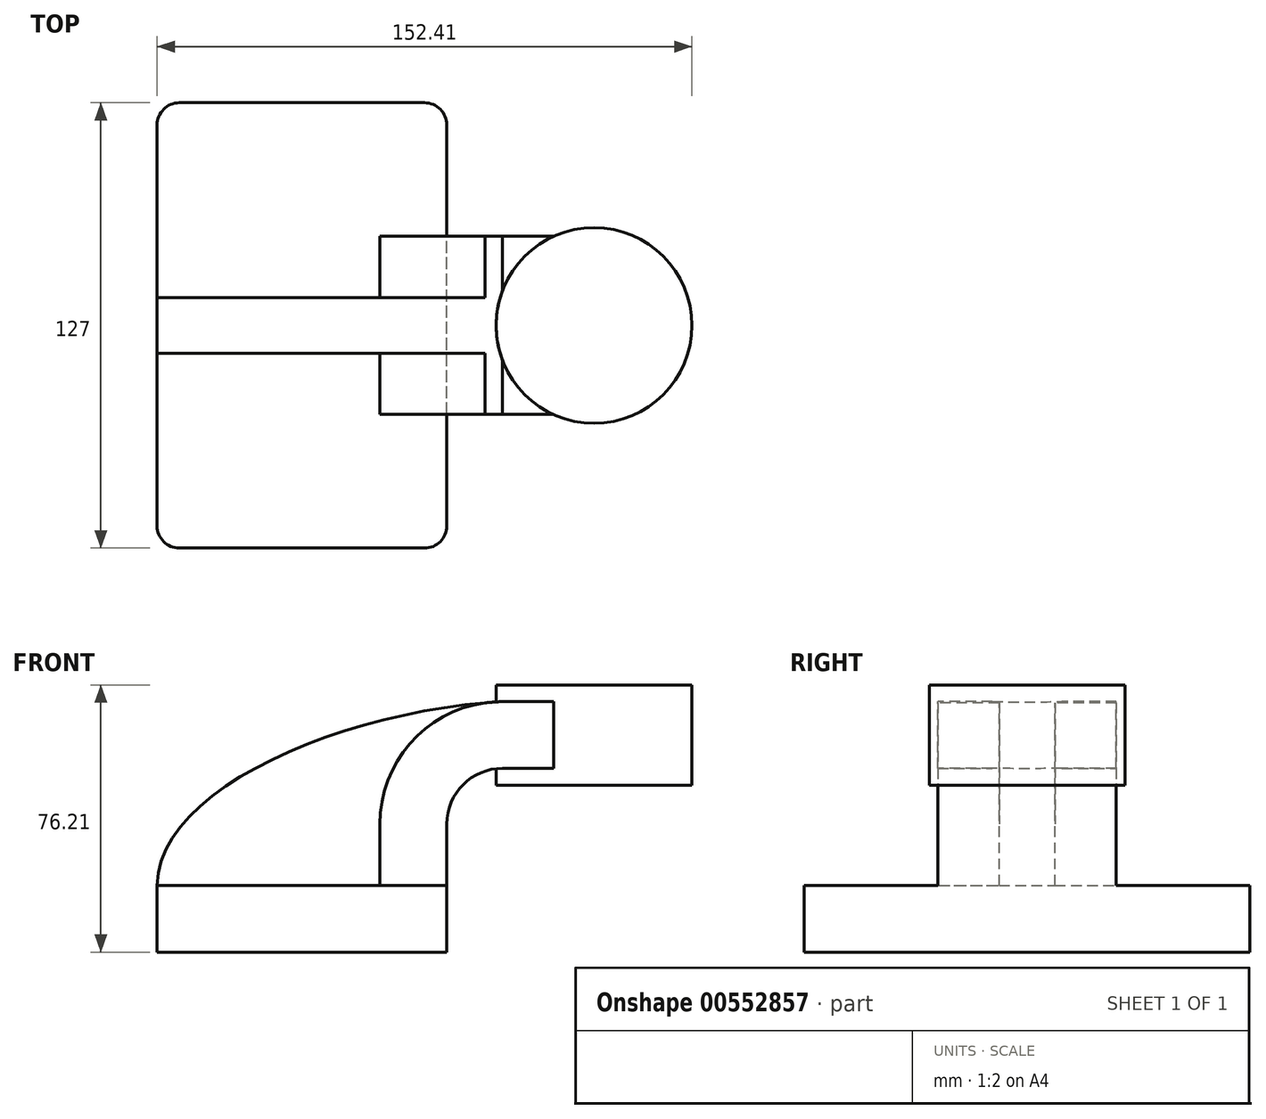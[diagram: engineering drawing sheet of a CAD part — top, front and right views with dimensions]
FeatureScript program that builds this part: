
annotation { "Feature Type Name" : "Feature", "Feature Type Description" : "" }
export const myFeature = defineFeature(function(context is Context, id is Id, definition is map)
    precondition{}
    {
        {
            var Q0;
            Q0=qCreatedBy(makeId("Front.planeOp"),FACE);
            var sketch = newSketch(context, id + "F0", { "sketchPlane" : qUnion([Q0])});
            skLineSegment(sketch, "E0.bottom", {"start": v(-41.28, 9.52) * mm, "end": v(41.27, 9.53) * mm});
            skLineSegment(sketch, "E0.top", {"start": v(-41.28, -9.53) * mm, "end": v(41.28, -9.53) * mm});
            skLineSegment(sketch, "E0.left", {"start": v(-41.28, 9.52) * mm, "end": v(-41.27, -9.53) * mm});
            skLineSegment(sketch, "E0.right", {"start": v(41.28, 9.53) * mm, "end": v(41.28, -9.52) * mm});
            skPoint(sketch, "E0.middle", {"position": v(0, 0) * mm});
            skLineSegment(sketch, "E1.bottom", {"start": v(60.32, 38.1) * mm, "end": v(111.12, 38.1) * mm});
            skLineSegment(sketch, "E1.top", {"start": v(60.32, 66.68) * mm, "end": v(111.12, 66.68) * mm});
            skLineSegment(sketch, "E1.left", {"start": v(60.32, 38.1) * mm, "end": v(60.32, 66.68) * mm});
            skLineSegment(sketch, "E1.right", {"start": v(111.12, 38.1) * mm, "end": v(111.12, 66.68) * mm});
            skPoint(sketch, "E1.middle", {"position": v(85.72, 52.39) * mm});
            skLineSegment(sketch, "E2", {"start": v(41.27, 9.53) * mm, "end": v(41.27, 27) * mm});
            skArc(sketch, "E3", {"start": v(41.27, 27) * mm, "mid": v(45.92, 38.23) * mm, "end": v(57.15, 42.88) * mm});
            skLineSegment(sketch, "E4", {"start": v(57.15, 42.88) * mm, "end": v(83.23, 42.88) * mm});
            skLineSegment(sketch, "E5.0", {"start": v(57.15, 61.93) * mm, "end": v(83.23, 61.93) * mm});
            skArc(sketch, "E5.1", {"start": v(22.22, 27) * mm, "mid": v(32.45, 51.7) * mm, "end": v(57.15, 61.93) * mm});
            skLineSegment(sketch, "E5.2", {"start": v(22.22, 9.53) * mm, "end": v(22.22, 27) * mm});
            skLineSegment(sketch, "E6", {"start": v(83.23, 61.93) * mm, "end": v(83.23, 42.88) * mm});
            skLineSegment(sketch, "E7", {"start": v(83.23, 38.1) * mm, "end": v(83.23, 42.88) * mm});
            skLineSegment(sketch, "E8", {"start": v(83.23, 61.93) * mm, "end": v(83.23, 66.68) * mm});
            skFitSpline(sketch, "E9", {"points": [v(-41.28, 9.52) * mm, v(57.15, 61.93) * mm], "startDerivative": vector(0.97, 83.3) * mm, "endDerivative": vector(135.74, 7.65) * mm});
            skSolve(sketch);
        }
        {
            var Q0;
            Q0=makeQuery(id+"F0.imprint","IMPRINT",FACE,{"disambiguationData":[TD([[makeQuery(id+"F0.imprint","IMPRINT",EDGE,{"derivedFrom":sQuery(id+"F0.wireOp",EDGE,"E0.top")}),1.0]])]});
            extrude(context, id + "F1", {"entities" : qUnion([Q0]), "endBound" : BoundingType.SYMMETRIC, "depth" : 127 * mm, "offsetDistance" : 25.4 * mm});
        }
        {
            var Q0;
            {var subQ1=sQuery(id+"F0.wireOp",EDGE,"E2");Q0=makeQuery(id+"F0.imprint","IMPRINT",FACE,{"disambiguationData":[TD([[makeQuery(id+"F0.imprint","IMPRINT",EDGE,{"derivedFrom":subQ1}),1.0]])]});}
            var Q1;
            {var subQ5=sQuery(id+"F0.wireOp",EDGE,"E6");Q1=makeQuery(id+"F0.imprint","IMPRINT",FACE,{"disambiguationData":[TD([[makeQuery(id+"F0.imprint","IMPRINT",EDGE,{"derivedFrom":subQ5}),-1.0]])]});}
            extrude(context, id + "F2", {"entities" : qUnion([Q0, Q1]), "operationType" : NewBodyOperationType.ADD, "endBound" : BoundingType.SYMMETRIC, "depth" : 50.8 * mm, "offsetDistance" : 25.4 * mm});
        }
        {
            var Q0;
            {var subQ3=sQuery(id+"F0.wireOp",EDGE,"E5.2");Q0=makeQuery(id+"F0.imprint","IMPRINT",FACE,{"disambiguationData":[TD([[makeQuery(id+"F0.imprint","IMPRINT",EDGE,{"derivedFrom":subQ3}),1.0]])]});}
            extrude(context, id + "F3", {"entities" : qUnion([Q0]), "operationType" : NewBodyOperationType.ADD, "endBound" : BoundingType.SYMMETRIC, "depth" : 15.88 * mm, "offsetDistance" : 25.4 * mm});
        }
        {
            var Q0;
            {var subQ0=sQuery(id+"F0.wireOp",EDGE,"E1.right");Q0=makeQuery(id+"F0.imprint","IMPRINT",FACE,{"disambiguationData":[TD([[makeQuery(id+"F0.imprint","IMPRINT",EDGE,{"derivedFrom":subQ0}),1.0]])]});}
            var Q1;
            Q1=sQuery(id+"F0.wireOp",EDGE,"E6");
            revolve(context, id + "F4", {"operationType" : NewBodyOperationType.ADD, "entities" : qUnion([Q0]), "axis" : qUnion([Q1]), "revolveType" : RevolveType.FULL});
        }
        {
            var Q0;
            Q0=makeQuery(id+"F1.opExtrude","CAP_EDGE",EDGE,{"disambiguationData":[OSD([sQuery(id+"F0.wireOp",EDGE,"E0.left")])],"isStart":false});
            var Q1;
            Q1=makeQuery(id+"F1.opExtrude","CAP_EDGE",EDGE,{"disambiguationData":[OSD([sQuery(id+"F0.wireOp",EDGE,"E0.right")])],"isStart":false});
            var Q2;
            Q2=makeQuery(id+"F1.opExtrude","CAP_EDGE",EDGE,{"disambiguationData":[OSD([sQuery(id+"F0.wireOp",EDGE,"E0.right")])],"isStart":true});
            var Q3;
            Q3=makeQuery(id+"F1.opExtrude","CAP_EDGE",EDGE,{"disambiguationData":[OSD([sQuery(id+"F0.wireOp",EDGE,"E0.left")])],"isStart":true});
            fillet(context, id + "F5", {"entities" : qUnion([Q0, Q1, Q2, Q3]), "radius" : 6.35 * mm, "tangentPropagation" : true, "allowEdgeOverflow" : false});
        }
    });
